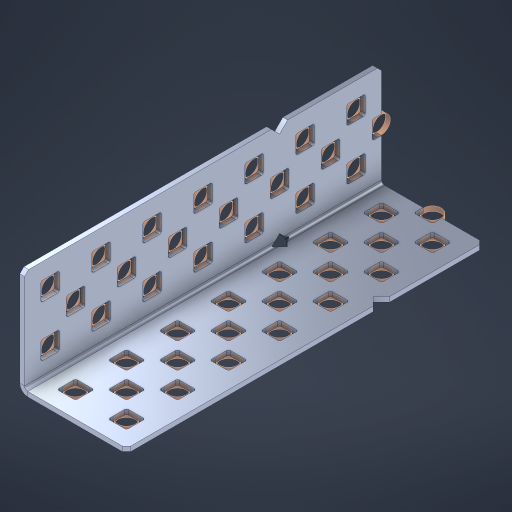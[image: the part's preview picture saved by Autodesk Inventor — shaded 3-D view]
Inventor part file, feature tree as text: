
AUTODESK INVENTOR PART (.ipt)
format: ipt  version: 2023 (Build 270158000, 158)  size: 798,720 bytes
history: native  units: in
note: dims shown in document units (in); Inventor stores cm internally (conversion verified against a paired STEP export)
features: other x48, extrude x40, sheet_metal_op x8, sketch x7, pattern_linear x2, mirror x1, chamfer x1
ambient origin geometry x8: Origin, YZ Plane, XZ Plane, XY Plane, X Axis, Y Axis, Z Axis, Center Point
bodies: Solid1 (feature_tree), Body (feature_tree)
feature tree (107):
  sheet_metal_op  "Flanges"
  sheet_metal_op  "Body Pattern"
  pattern_linear  "Center Pattern"  Spacing1=1.0in  [1 undecoded]
  other  "Arc Length"
  pattern_linear  "Notch Pattern"  Spacing1=0.1875in  [1 undecoded]
  other  "Diagonal Plane"
  mirror  "Everything Mirrored"
  chamfer  "End Chamfer"
  sketch  "Sketch1"  dims[d0=1.0in]
  other  "Plate1"
  sketch  "Sketch2"  dims[d1=3.5in]
  other  "Plate2"
  sheet_metal_op  "Bend1"
  sheet_metal_op  "Corner1"
  sketch  "Sketch8"  dims[d2=0.0469in]
  sketch  "Sketch9"  dims[d3=0.0469in]
  other  "Srf91"
  sheet_metal_op  "Body Pattern Sketch"
  other  "Srf92"
  sketch  "Sketch13"  dims[d4=0.0234in]
  sketch  "Sketch15"  dims[d5=0.0938in]
  sketch  "Sketch16"  dims[d6=0.0469in d7=1.0in d8=90.0deg d9=0.0312in d10=0.1875in d11=0.0469in d12=0.0469in d49=0.182in d50=0.02in d52=0.25in d53=0.0469in d54=0.0in d55=0.172in d56=1.0in d57=0.0in d60=2.7559in d62=0.5in d63=0.7874in d65=0.5in d85=0.1473in d86=0.1659in d89=0.0469in d90=0.0in d91=0.04in d92=0.0491in d95=2.5in d96=0.04in d97=0.25in d98=45.0deg d99=0.25in d106=0.182in d107=0.02in d108=0.5in d110=0.0469in d111=0.0in d112=0.172in d113=0.5in d114=0.0in d117=0.5in d123=0.25in d125=0.25in d126=0.0491in d127=0.1227in d128=0.08in d129=0.04in d130=2.5in]
  other  "Srf786"
  other  "Srf856"
  other  "Srf857"
  other  "Srf858"
  other  "Srf859"
  other  "Srf860"
  other  "Srf861"
  other  "Srf889"
  other  "Srf890"
  other  "Srf891"
  other  "Srf1275"
  other  "Srf1276"
  other  "Srf1278"
  other  "Srf1279"
  other  "Srf1280"
  other  "Srf1281"
  other  "Srf1282"
  other  "Srf1283"
  other  "Srf1277"
  other  "Srf1285"
  other  "Srf1286"
  other  "Srf1287"
  other  "Srf1383"
  other  "Srf1384"
  other  "Srf1385"
  other  "Srf1386"
  other  "Srf1387"
  other  "Srf1388"
  other  "Srf1445"
  other  "Srf1446"
  other  "Srf1447"
  other  "Srf1475"
  other  "Srf1476"
  other  "Srf1477"
  other  "Srf1478"
  other  "Srf1479"
  other  "Srf1480"
  other  "Srf1537"
  other  "Srf1538"
  other  "Srf1539"
  sheet_metal_op  "Body Stamp"
  sheet_metal_op  "Body Circle"
  other  "Center Stamp"
  other  "Center Circle"
  sheet_metal_op  "Notch"
  extrude  "ExtrusionSrf92"  Depth=0.0469in
  extrude  "ExtrusionSrf856"  Depth=0.0469in
  extrude  "ExtrusionSrf857"  Depth=0.182in
  extrude  "ExtrusionSrf858"  Depth=0.02in
  extrude  "ExtrusionSrf859"  Depth=0.25in
  extrude  "ExtrusionSrf860"  Depth=0.0469in
  extrude  "ExtrusionSrf861"  TaperAngle=0.0deg  [1 undecoded]
  extrude  "ExtrusionSrf889"  Depth=2.5in
  extrude  "ExtrusionSrf890"  Depth=1.0in TaperAngle=0.0deg
  extrude  "ExtrusionSrf891"  Depth=2.5in
  extrude  "ExtrusionSrf1275"  Depth=0.5in
  extrude  "ExtrusionSrf1276"  Depth=2.5in
  extrude  "ExtrusionSrf1277"  Depth=2.5in
  extrude  "ExtrusionSrf1278"  Depth=0.0469in
  extrude  "ExtrusionSrf1279"  Depth=2.5in TaperAngle=0.0deg
  extrude  "ExtrusionSrf1280"  Depth=2.5in
  extrude  "ExtrusionSrf1281"  Depth=0.25in TaperAngle=45.0deg
  extrude  "ExtrusionSrf1282"  Depth=0.25in
  extrude  "ExtrusionSrf1345"  Depth=0.182in
  extrude  "ExtrusionSrf1346"  Depth=0.02in
  extrude  "ExtrusionSrf1347"  Depth=0.5in
  extrude  "ExtrusionSrf1348"  Depth=0.0469in
  extrude  "ExtrusionSrf1383"  TaperAngle=0.0deg  [1 undecoded]
  extrude  "ExtrusionSrf1384"  Depth=2.5in
  extrude  "ExtrusionSrf1385"  Depth=0.5in TaperAngle=0.0deg
  extrude  "ExtrusionSrf1386"  Depth=0.5in
  extrude  "ExtrusionSrf1387"  Depth=0.25in
  extrude  "ExtrusionSrf1388"  Depth=0.25in
  extrude  "ExtrusionSrf1445"  Depth=2.5in
  extrude  "ExtrusionSrf1446"  Depth=2.5in
  extrude  "ExtrusionSrf1447"  Depth=2.5in
  extrude  "ExtrusionSrf1475"  Depth=2.5in
  extrude  "ExtrusionSrf1476"  Depth=2.5in
  extrude  "ExtrusionSrf1477"  [1 undecoded]
  extrude  "ExtrusionSrf1478"  [1 undecoded]
  extrude  "ExtrusionSrf1479"  [1 undecoded]
  extrude  "ExtrusionSrf1480"  [1 undecoded]
  extrude  "ExtrusionSrf1537"  [1 undecoded]
  extrude  "ExtrusionSrf1538"  [1 undecoded]
  extrude  "ExtrusionSrf1539"  [1 undecoded]
note: 11 required parameter values undecoded (feature->parameter linkage not recoverable at this tier; creation-order binding heuristic only, values carry confidence <= 0.55)
